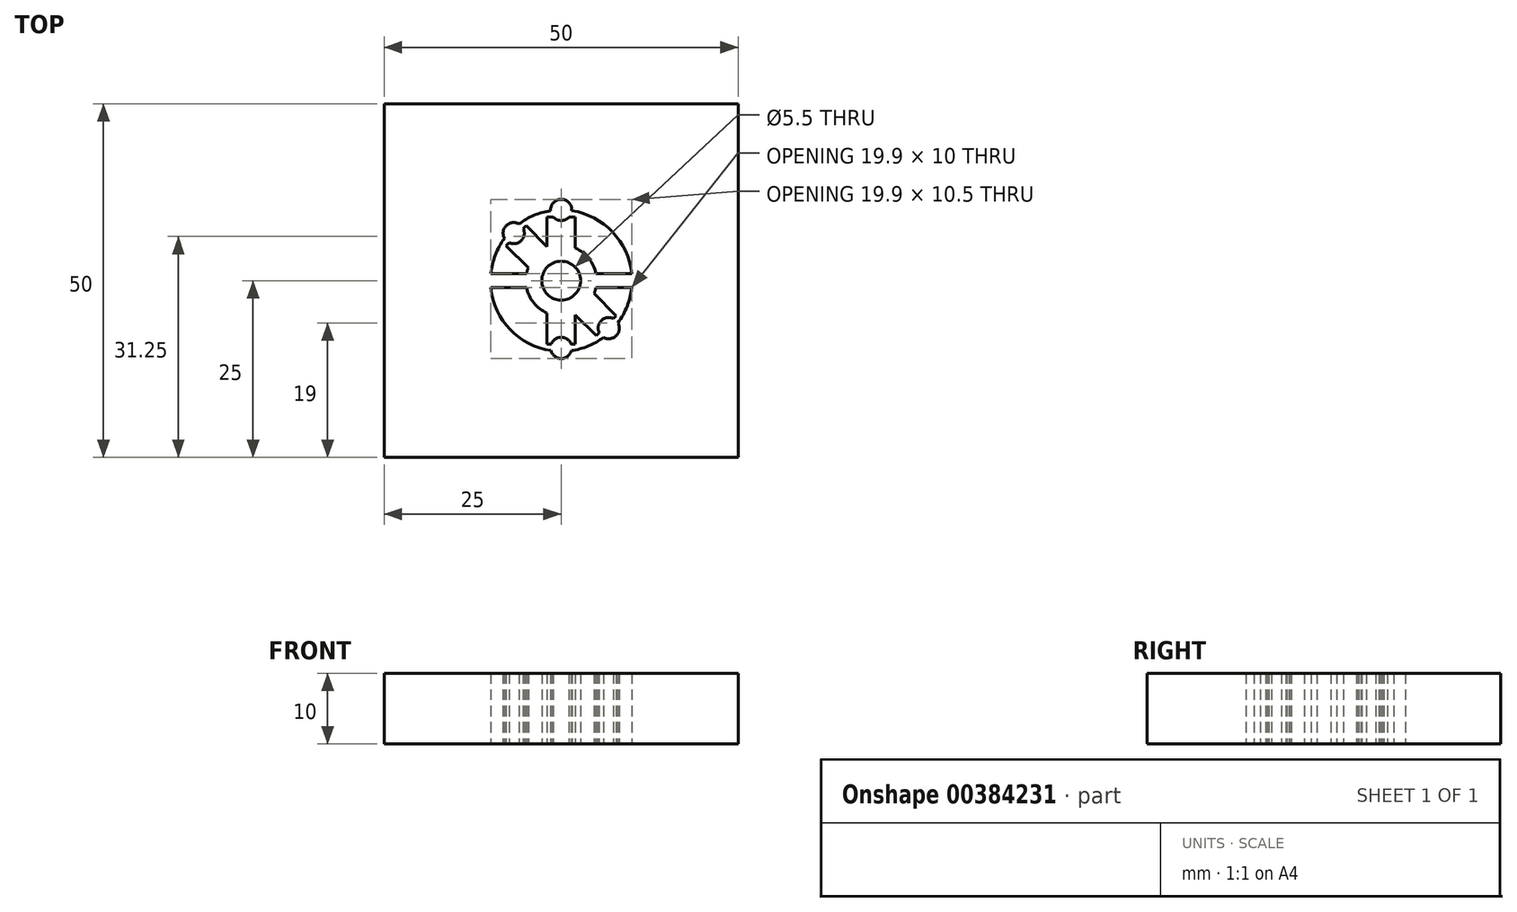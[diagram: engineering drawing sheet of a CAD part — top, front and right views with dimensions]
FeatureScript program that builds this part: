
annotation { "Feature Type Name" : "Feature", "Feature Type Description" : "" }
export const myFeature = defineFeature(function(context is Context, id is Id, definition is map)
    precondition{}
    {
        {
            var Q0;
            Q0=qCreatedBy(makeId("Top.planeOp"),FACE);
            var sketch = newSketch(context, id + "F0", { "sketchPlane" : qUnion([Q0])});
            skLineSegment(sketch, "E0.bottom", {"start": v(-25, 25) * mm, "end": v(25, 25) * mm});
            skLineSegment(sketch, "E0.top", {"start": v(-25, -25) * mm, "end": v(25, -25) * mm});
            skLineSegment(sketch, "E0.left", {"start": v(-25, 25) * mm, "end": v(-25, -25) * mm});
            skLineSegment(sketch, "E0.right", {"start": v(25, 25) * mm, "end": v(25, -25) * mm});
            skSolve(sketch);
        }
        {
            var Q0;
            Q0 = qSketchRegion(id + "F0", true);
            extrude(context, id + "F1", {"entities" : qUnion([Q0]), "depth" : 10 * mm});
        }
        {
            var Q0;
            Q0=qCreatedBy(makeId("Top.planeOp"),FACE);
            var sketch = newSketch(context, id + "F2", { "sketchPlane" : qUnion([Q0])});
            skArc(sketch, "E1", {"start": v(-9.95, -1) * mm, "mid": v(0, -10) * mm, "end": v(9.95, -1) * mm});
            skArc(sketch, "E2", {"start": v(-4.9, -1) * mm, "mid": v(0, -5) * mm, "end": v(4.9, -1) * mm});
            skLineSegment(sketch, "E3", {"start": v(-9.95, 1) * mm, "end": v(-4.9, 1) * mm});
            skLineSegment(sketch, "E4", {"start": v(-9.95, -1) * mm, "end": v(-4.9, -1) * mm});
            skLineSegment(sketch, "E5.trimOffspring", {"start": v(4.9, -1) * mm, "end": v(9.95, -1) * mm});
            skLineSegment(sketch, "E6.trimOffspring", {"start": v(4.9, 1) * mm, "end": v(9.95, 1) * mm});
            skArc(sketch, "E7.trimOffspring", {"start": v(4.9, 1) * mm, "mid": v(0, 5) * mm, "end": v(-4.9, 1) * mm});
            skArc(sketch, "E8.trimOffspring", {"start": v(9.95, 1) * mm, "mid": v(0, 10) * mm, "end": v(-9.95, 1) * mm});
            skSolve(sketch);
        }
        {
            var Q0;
            Q0 = qSketchRegion(id + "F2", true);
            extrude(context, id + "F3", {"entities" : qUnion([Q0]), "operationType" : NewBodyOperationType.REMOVE, "endBound" : BoundingType.UP_TO_NEXT, "depth" : 25.4 * mm});
        }
        {
            var Q0;
            Q0=qCreatedBy(makeId("Top.planeOp"),FACE);
            var sketch = newSketch(context, id + "F4", { "sketchPlane" : qUnion([Q0])});
            skPoint(sketch, "E9", {"position": v(-6.72, 6.72) * mm});
            skPoint(sketch, "E10", {"position": v(0, 9.5) * mm});
            skPoint(sketch, "E11", {"position": v(0, 10) * mm});
            skLineSegment(sketch, "E12", {"start": v(-32.8, 32.8) * mm, "end": v(64.8, -64.8) * mm, "construction": true});
            skLineSegment(sketch, "E13.bottom", {"start": v(-2, 9) * mm, "end": v(2, 9) * mm});
            skLineSegment(sketch, "E13.top", {"start": v(-2, -9) * mm, "end": v(2, -9) * mm});
            skLineSegment(sketch, "E13.left", {"start": v(2, 9) * mm, "end": v(2, -9) * mm});
            skLineSegment(sketch, "E13.right", {"start": v(-2, 9) * mm, "end": v(-2, -9) * mm});
            skLineSegment(sketch, "E14.bottom", {"start": v(-7.78, 4.95) * mm, "end": v(-4.95, 7.78) * mm});
            skLineSegment(sketch, "E14.top", {"start": v(4.95, -7.78) * mm, "end": v(7.78, -4.95) * mm});
            skLineSegment(sketch, "E14.left", {"start": v(-7.78, 4.95) * mm, "end": v(4.95, -7.78) * mm});
            skLineSegment(sketch, "E14.right", {"start": v(-4.95, 7.78) * mm, "end": v(7.78, -4.95) * mm});
            skLineSegment(sketch, "E15", {"start": v(-9.07, -9.07) * mm, "end": v(14.28, 14.28) * mm, "construction": true});
            skCircle(sketch, "E16", {"center": v(0, 0) * mm, "radius": 9.5 * mm, "construction": true});
            skPoint(sketch, "E17", {"position": v(0, -9.5) * mm});
            skPoint(sketch, "E18", {"position": v(6.72, -6.72) * mm});
            skSolve(sketch);
        }
        {
            var Q0;
            Q0 = qSketchRegion(id + "F4", true);
            extrude(context, id + "F5", {"entities" : qUnion([Q0]), "operationType" : NewBodyOperationType.ADD, "depth" : 10 * mm});
        }
        {
            var Q0;
            Q0=qCreatedBy(makeId("Top.planeOp"),FACE);
            var sketch = newSketch(context, id + "F6", { "sketchPlane" : qUnion([Q0])});
            skPoint(sketch, "E19", {"position": v(0, 0) * mm});
            skSolve(sketch);
        }
        {
            var Q0;
            Q0=sQuery(id+"F6.wireOp",VERTEX,"E19");
            var Q1;
            Q1=makeQuery(id+"F1.opExtrude","SWEPT_BODY",BODY,{"disambiguationData":[OSD([sQuery(id+"F0.wireOp",EDGE,"E0.bottom"),sQuery(id+"F0.wireOp",EDGE,"E0.top"),sQuery(id+"F0.wireOp",EDGE,"E0.left"),sQuery(id+"F0.wireOp",EDGE,"E0.right")])]});
            hole(context, id + "F7", {"style" : HoleStyle.SIMPLE, "endStyle" : HoleEndStyle.THROUGH, "oppositeDirection" : true, "holeDiameter" : 5.5 * mm, "isTappedThrough" : true, "tappedDepth" : 12.7 * mm, "tapClearance" : 3, "locations" : qUnion([Q0]), "scope" : qUnion([Q1])});
        }
        {
            var Q0;
            Q0=sQuery(id+"F4.wireOp",VERTEX,"E9");
            var Q1;
            Q1=sQuery(id+"F4.wireOp",VERTEX,"E11");
            var Q2;
            Q2=sQuery(id+"F4.wireOp",VERTEX,"E17");
            var Q3;
            Q3=sQuery(id+"F4.wireOp",VERTEX,"E18");
            var Q4;
            Q4=makeQuery(id+"F1.opExtrude","SWEPT_BODY",BODY,{"disambiguationData":[OSD([sQuery(id+"F0.wireOp",EDGE,"E0.bottom"),sQuery(id+"F0.wireOp",EDGE,"E0.top"),sQuery(id+"F0.wireOp",EDGE,"E0.left"),sQuery(id+"F0.wireOp",EDGE,"E0.right")])]});
            hole(context, id + "F8", {"style" : HoleStyle.SIMPLE, "endStyle" : HoleEndStyle.THROUGH, "oppositeDirection" : true, "holeDiameter" : 3 * mm, "isTappedThrough" : true, "tappedDepth" : 12.7 * mm, "tapClearance" : 3, "locations" : qUnion([Q0, Q1, Q2, Q3]), "scope" : qUnion([Q4])});
        }
    });
